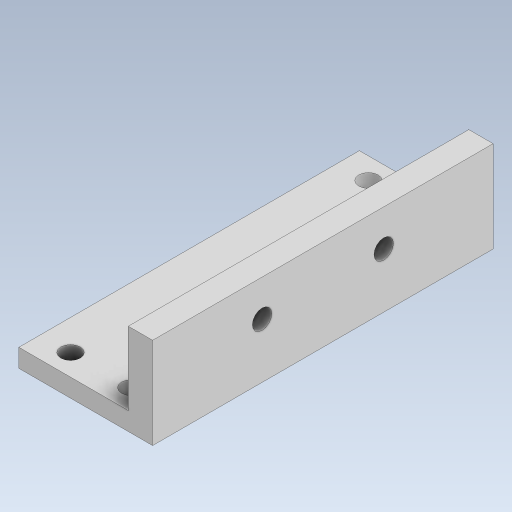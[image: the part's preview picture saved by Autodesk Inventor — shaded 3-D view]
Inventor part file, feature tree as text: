
AUTODESK INVENTOR PART (.ipt)
format: ipt  version: 2023.5 (Build 275446000, 446)  size: 278,016 bytes
history: native  units: mm
features: extrude x3, sketch x2
ambient origin geometry x8: Origin, YZ Plane, XZ Plane, XY Plane, X Axis, Y Axis, Z Axis, Center Point
bodies: Solid1 (feature_tree)
feature tree (5):
  sketch  "Sketch1"  dims[d0=3.2mm d2=24.5mm]
  extrude  "Extrusion1"  Depth=24.5mm
  extrude  "Extrusion2"  Depth=3.0mm TaperAngle=0.0deg
  extrude  "Extrusion3"  Depth=10.0mm
  sketch  "Sketch2"  dims[d3=5.0mm d4=3.0mm d5=0.0mm d6=2.0mm d7=15.0mm d8=0.0mm d9=3.2mm d10=5.5mm d11=15.0mm d12=0.0mm d13=10.0mm d15=0.5mm d16=0.872665mm d17=0.5mm d18=0.872665mm]
